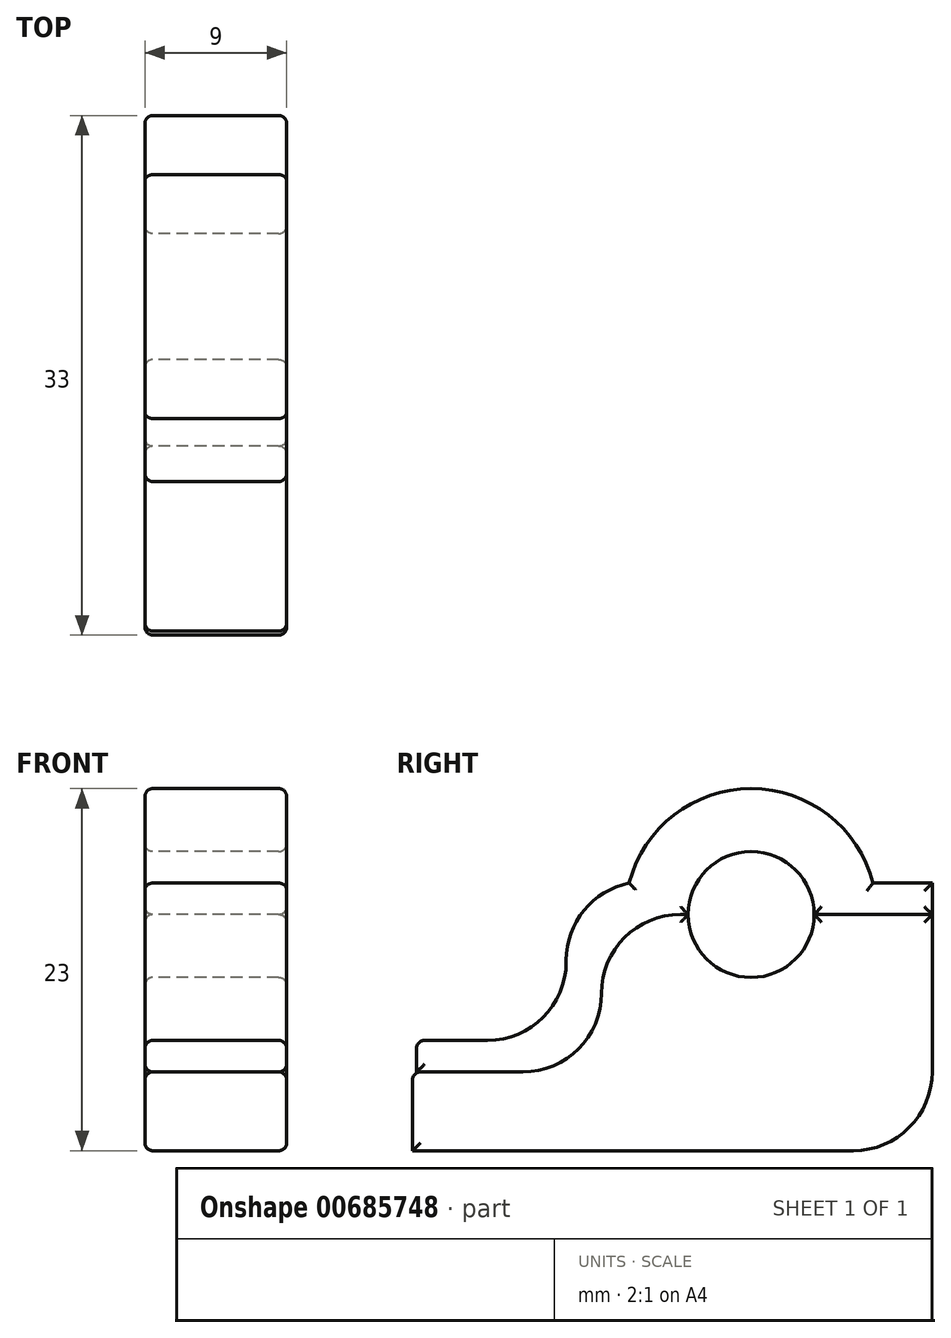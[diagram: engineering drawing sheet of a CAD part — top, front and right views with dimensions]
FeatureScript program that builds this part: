
annotation { "Feature Type Name" : "Feature", "Feature Type Description" : "" }
export const myFeature = defineFeature(function(context is Context, id is Id, definition is map)
    precondition{}
    {
        {
            var Q0;
            Q0=qCreatedBy(makeId("Right.planeOp"),FACE);
            var sketch = newSketch(context, id + "F0", { "sketchPlane" : qUnion([Q0])});
            skCircle(sketch, "E0", {"center": v(0, 12) * mm, "radius": 4 * mm});
            skLineSegment(sketch, "E1", {"start": v(-9.5, 12) * mm, "end": v(-9.5, 2) * mm});
            skLineSegment(sketch, "E2", {"start": v(-9.5, 2) * mm, "end": v(-21.5, 2) * mm});
            skLineSegment(sketch, "E3", {"start": v(-21.5, 2) * mm, "end": v(-21.5, 0) * mm});
            skLineSegment(sketch, "E4", {"start": v(11.5, -3) * mm, "end": v(11.5, 12) * mm});
            skLineSegment(sketch, "E5", {"start": v(11.5, 12) * mm, "end": v(4, 12) * mm});
            skLineSegment(sketch, "E6", {"start": v(-4, 12) * mm, "end": v(-9.5, 12) * mm});
            skArc(sketch, "E7.0", {"start": v(7.75, 14) * mm, "mid": v(0, 20) * mm, "end": v(-7.75, 14) * mm});
            skLineSegment(sketch, "E8", {"start": v(11.5, 12) * mm, "end": v(11.5, 14) * mm});
            skLineSegment(sketch, "E9", {"start": v(11.5, 14) * mm, "end": v(7.75, 14) * mm});
            skLineSegment(sketch, "E10", {"start": v(-7.75, 14) * mm, "end": v(-11.75, 14) * mm});
            skLineSegment(sketch, "E11", {"start": v(-11.75, 14) * mm, "end": v(-11.75, 4) * mm});
            skLineSegment(sketch, "E12", {"start": v(-11.75, 4) * mm, "end": v(-21.25, 4) * mm});
            skLineSegment(sketch, "E13", {"start": v(-21.25, 4) * mm, "end": v(-21.25, 2) * mm});
            skLineSegment(sketch, "E14", {"start": v(11.5, -3) * mm, "end": v(-21.5, -3) * mm});
            skLineSegment(sketch, "E15", {"start": v(-21.5, -3) * mm, "end": v(-21.5, 0) * mm});
            skSolve(sketch);
        }
        {
            var Q0;
            Q0=makeQuery(id+"F0.imprint","IMPRINT",FACE,{"disambiguationData":[TD([[makeQuery(id+"F0.imprint","IMPRINT",EDGE,{"derivedFrom":sQuery(id+"F0.wireOp",EDGE,"E1")}),1.0]])]});
            extrude(context, id + "F1", {"entities" : qUnion([Q0]), "depth" : 9 * mm, "offsetDistance" : 25 * mm});
        }
        {
            var Q0;
            Q0=makeQuery(id+"F1.opExtrude","SWEPT_EDGE",EDGE,{"disambiguationData":[OSD([sQuery(id+"F0.wireOp",EDGE,"E1"),sQuery(id+"F0.wireOp",EDGE,"E2")])]});
            fillet(context, id + "F2", {"entities" : qUnion([Q0]), "radius" : 5 * mm, "tangentPropagation" : true, "allowEdgeOverflow" : false});
        }
        {
            var Q0;
            Q0=makeQuery(id+"F1.opExtrude","CAP_FACE",FACE,{"disambiguationData":[OSD([sQuery(id+"F0.wireOp",EDGE,"E0"),sQuery(id+"F0.wireOp",EDGE,"E1"),sQuery(id+"F0.wireOp",EDGE,"E2"),sQuery(id+"F0.wireOp",EDGE,"E3"),sQuery(id+"F0.wireOp",EDGE,"XKc3wIS3-Ej8d-IZYB-obh2-cHktmvv2Logo"),sQuery(id+"F0.wireOp",EDGE,"E4"),sQuery(id+"F0.wireOp",EDGE,"E5"),sQuery(id+"F0.wireOp",EDGE,"E6")])],"isStart":true});
            var Q1;
            Q1=makeQuery(id+"F1.opExtrude","CAP_FACE",FACE,{"disambiguationData":[OSD([sQuery(id+"F0.wireOp",EDGE,"E0"),sQuery(id+"F0.wireOp",EDGE,"E1"),sQuery(id+"F0.wireOp",EDGE,"E2"),sQuery(id+"F0.wireOp",EDGE,"E3"),sQuery(id+"F0.wireOp",EDGE,"XKc3wIS3-Ej8d-IZYB-obh2-cHktmvv2Logo"),sQuery(id+"F0.wireOp",EDGE,"E4"),sQuery(id+"F0.wireOp",EDGE,"E5"),sQuery(id+"F0.wireOp",EDGE,"E6")])],"isStart":false});
            var Q2;
            Q2=makeQuery(id+"F1.opExtrude","SWEPT_EDGE",EDGE,{"disambiguationData":[OSD([sQuery(id+"F0.wireOp",EDGE,"E2"),sQuery(id+"F0.wireOp",EDGE,"E3")])]});
            fillet(context, id + "F3", {"entities" : qUnion([Q0, Q1, Q2]), "radius" : 0.5 * mm, "tangentPropagation" : true, "allowEdgeOverflow" : false});
        }
        {
            var Q0;
            {var subQ3=sQuery(id+"F0.wireOp",EDGE,"E1");Q0=makeQuery(id+"F0.imprint","IMPRINT",FACE,{"disambiguationData":[TD([[makeQuery(id+"F0.imprint","IMPRINT",EDGE,{"derivedFrom":subQ3}),-1.0]])]});}
            extrude(context, id + "F4", {"entities" : qUnion([Q0]), "depth" : 9 * mm, "offsetDistance" : 25 * mm});
        }
        {
            var Q0;
            Q0=makeQuery(id+"F4.opExtrude","SWEPT_EDGE",EDGE,{"disambiguationData":[OSD([sQuery(id+"F0.wireOp",EDGE,"E1"),sQuery(id+"F0.wireOp",EDGE,"E2")])]});
            var Q1;
            Q1=makeQuery(id+"F4.opExtrude","SWEPT_EDGE",EDGE,{"disambiguationData":[OSD([sQuery(id+"F0.wireOp",EDGE,"E11"),sQuery(id+"F0.wireOp",EDGE,"E12")])]});
            var Q2;
            Q2=makeQuery(id+"F4.opExtrude","SWEPT_EDGE",EDGE,{"disambiguationData":[OSD([sQuery(id+"F0.wireOp",EDGE,"E1"),sQuery(id+"F0.wireOp",EDGE,"E6")])]});
            var Q3;
            Q3=makeQuery(id+"F4.opExtrude","SWEPT_EDGE",EDGE,{"disambiguationData":[OSD([sQuery(id+"F0.wireOp",EDGE,"E10"),sQuery(id+"F0.wireOp",EDGE,"E11")])]});
            fillet(context, id + "F5", {"entities" : qUnion([Q0, Q1, Q2, Q3]), "radius" : 5 * mm, "tangentPropagation" : true, "allowEdgeOverflow" : false});
        }
        {
            var Q0;
            Q0=makeQuery(id+"F1.opExtrude","SWEPT_EDGE",EDGE,{"disambiguationData":[OSD([sQuery(id+"F0.wireOp",EDGE,"E1"),sQuery(id+"F0.wireOp",EDGE,"E6")])]});
            fillet(context, id + "F6", {"entities" : qUnion([Q0]), "radius" : 5 * mm, "tangentPropagation" : true, "allowEdgeOverflow" : false});
        }
        {
            var Q0;
            Q0=makeQuery(id+"F1.opExtrude","SWEPT_EDGE",EDGE,{"disambiguationData":[OSD([sQuery(id+"F0.wireOp",EDGE,"XKc3wIS3-Ej8d-IZYB-obh2-cHktmvv2Logo"),sQuery(id+"F0.wireOp",EDGE,"E4")])]});
            fillet(context, id + "F7", {"entities" : qUnion([Q0]), "radius" : 5 * mm, "tangentPropagation" : true, "allowEdgeOverflow" : false});
        }
        {
            var Q0;
            Q0=makeQuery(id+"F4.opExtrude","CAP_FACE",FACE,{"disambiguationData":[OSD([sQuery(id+"F0.wireOp",EDGE,"E0"),sQuery(id+"F0.wireOp",EDGE,"E1"),sQuery(id+"F0.wireOp",EDGE,"E2"),sQuery(id+"F0.wireOp",EDGE,"E5"),sQuery(id+"F0.wireOp",EDGE,"E6"),sQuery(id+"F0.wireOp",EDGE,"E7.0"),sQuery(id+"F0.wireOp",EDGE,"E8"),sQuery(id+"F0.wireOp",EDGE,"E9"),sQuery(id+"F0.wireOp",EDGE,"E10"),sQuery(id+"F0.wireOp",EDGE,"E11"),sQuery(id+"F0.wireOp",EDGE,"E12"),sQuery(id+"F0.wireOp",EDGE,"E13")])],"isStart":false});
            var Q1;
            Q1=makeQuery(id+"F4.opExtrude","CAP_FACE",FACE,{"disambiguationData":[OSD([sQuery(id+"F0.wireOp",EDGE,"E0"),sQuery(id+"F0.wireOp",EDGE,"E1"),sQuery(id+"F0.wireOp",EDGE,"E2"),sQuery(id+"F0.wireOp",EDGE,"E5"),sQuery(id+"F0.wireOp",EDGE,"E6"),sQuery(id+"F0.wireOp",EDGE,"E7.0"),sQuery(id+"F0.wireOp",EDGE,"E8"),sQuery(id+"F0.wireOp",EDGE,"E9"),sQuery(id+"F0.wireOp",EDGE,"E10"),sQuery(id+"F0.wireOp",EDGE,"E11"),sQuery(id+"F0.wireOp",EDGE,"E12"),sQuery(id+"F0.wireOp",EDGE,"E13")])],"isStart":true});
            var Q2;
            Q2=makeQuery(id+"F4.opExtrude","SWEPT_FACE",FACE,{"disambiguationData":[OSD([sQuery(id+"F0.wireOp",EDGE,"E12")])]});
            fillet(context, id + "F8", {"entities" : qUnion([Q0, Q1, Q2]), "radius" : 0.5 * mm, "tangentPropagation" : true, "allowEdgeOverflow" : false});
        }
    });
